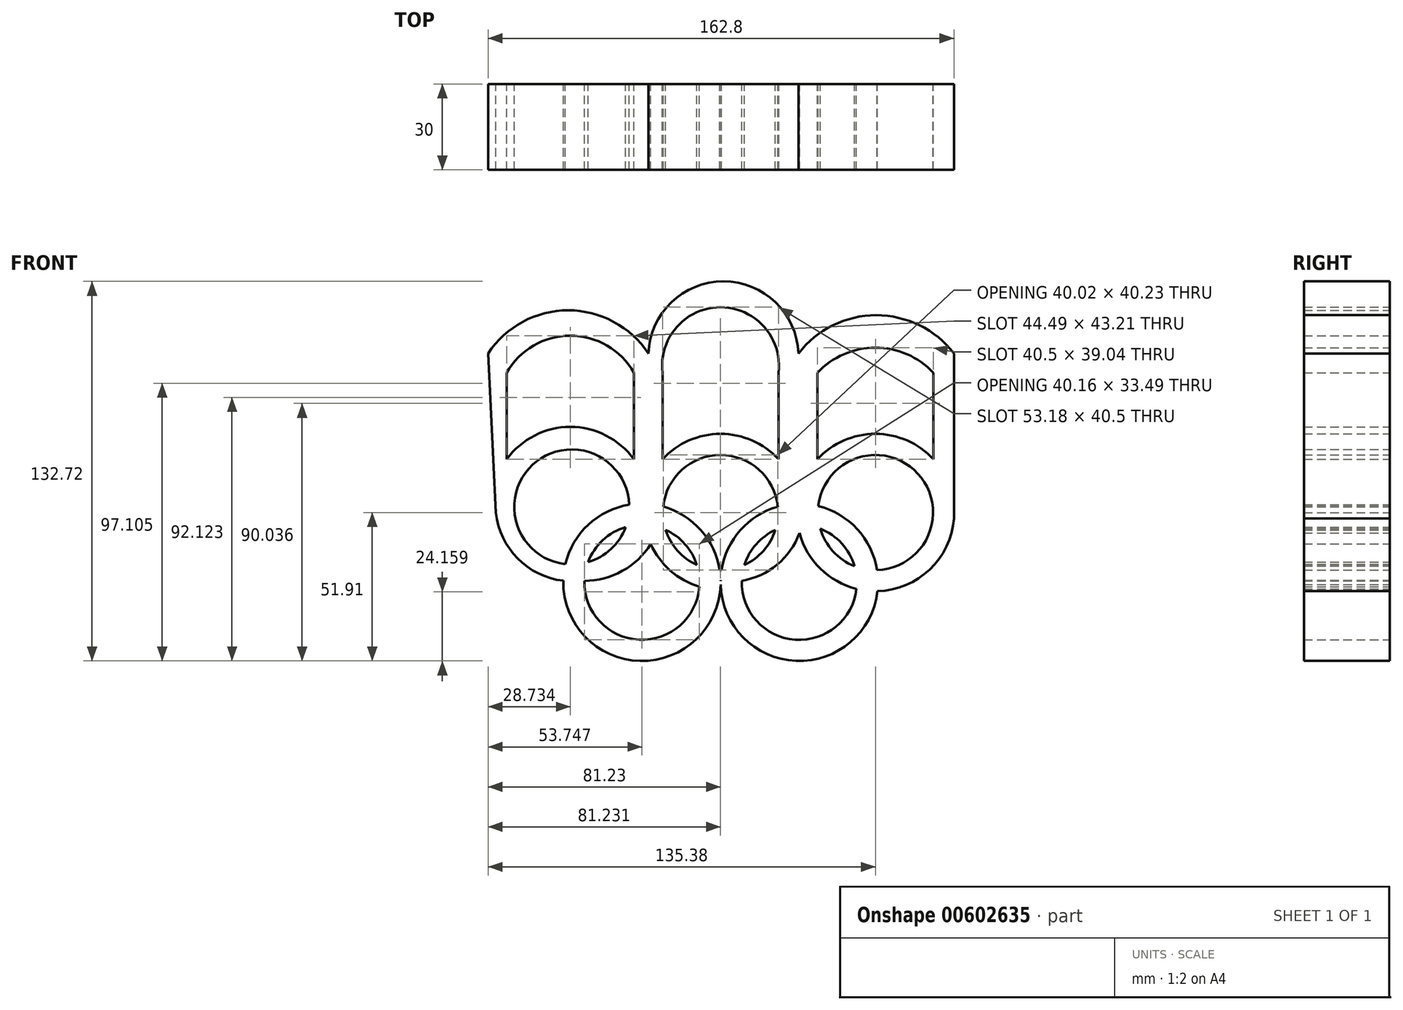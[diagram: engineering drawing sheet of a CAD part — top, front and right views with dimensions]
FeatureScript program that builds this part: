
annotation { "Feature Type Name" : "Feature", "Feature Type Description" : "" }
export const myFeature = defineFeature(function(context is Context, id is Id, definition is map)
    precondition{}
    {
        {
            var Q0;
            Q0=qCreatedBy(makeId("Front.planeOp"),FACE);
            var sketch = newSketch(context, id + "F0", { "sketchPlane" : qUnion([Q0])});
            skArc(sketch, "E0", {"start": v(-19.17, -6.08) * mm, "mid": v(-15.03, -13.36) * mm, "end": v(-8.28, -18.33) * mm});
            skArc(sketch, "E1", {"start": v(27.6, -7.19) * mm, "mid": v(34.9, -19.64) * mm, "end": v(47.5, -26.69) * mm});
            skArc(sketch, "E2", {"start": v(34.85, -5.68) * mm, "mid": v(39.32, -13.6) * mm, "end": v(46.82, -18.73) * mm});
            skArc(sketch, "E3", {"start": v(-31.88, 2.74) * mm, "mid": v(-65.68, 16.66) * mm, "end": v(-54.21, -18.05) * mm});
            skArc(sketch, "E4", {"start": v(-26.04, 3.06) * mm, "mid": v(-26.68, 3.08) * mm, "end": v(-27.33, 3.1) * mm});
            skArc(sketch, "E5", {"start": v(-26.39, -4.32) * mm, "mid": v(-26.47, -4.32) * mm, "end": v(-26.55, -4.31) * mm});
            skArc(sketch, "E6", {"start": v(0.03, -23.66) * mm, "mid": v(25.6, -51.84) * mm, "end": v(54.85, -27.5) * mm});
            skArc(sketch, "E7", {"start": v(7.42, -23.85) * mm, "mid": v(26.1, -44.47) * mm, "end": v(47.5, -26.69) * mm});
            skArc(sketch, "E8.trimOffspring", {"start": v(-31.88, 2.74) * mm, "mid": v(-46.2, -4.28) * mm, "end": v(-54.21, -18.05) * mm});
            skArc(sketch, "E9.trimOffspring", {"start": v(-33.14, -5.11) * mm, "mid": v(-41.16, -9.68) * mm, "end": v(-46.3, -17.36) * mm});
            skArc(sketch, "E10.trimOffspring", {"start": v(-47.56, -23.87) * mm, "mid": v(-28.48, -44.5) * mm, "end": v(-7.4, -25.92) * mm});
            skArc(sketch, "E11.trimOffspring", {"start": v(-46.3, -17.36) * mm, "mid": v(-38.27, -12.79) * mm, "end": v(-33.14, -5.11) * mm});
            skArc(sketch, "E12.trimOffspring", {"start": v(-54.95, -23.85) * mm, "mid": v(-27.36, -51.9) * mm, "end": v(0.03, -23.66) * mm});
            skArc(sketch, "E13.trimOffspring", {"start": v(-47.56, -23.87) * mm, "mid": v(-34.32, -20.42) * mm, "end": v(-24.38, -11) * mm});
            skArc(sketch, "E14.trimOffspring", {"start": v(-8.28, -18.33) * mm, "mid": v(-12.42, -11.04) * mm, "end": v(-19.17, -6.08) * mm});
            skArc(sketch, "E15.trimOffspring", {"start": v(-0.3, -20.11) * mm, "mid": v(0.03, -20.11) * mm, "end": v(0.36, -20.11) * mm});
            skArc(sketch, "E16.trimOffspring", {"start": v(0.03, -23.88) * mm, "mid": v(0.03, -23.88) * mm, "end": v(0.04, -23.88) * mm});
            skArc(sketch, "E17.trimOffspring", {"start": v(-0.3, -20.11) * mm, "mid": v(-6.9, -6.14) * mm, "end": v(-20, 2.07) * mm});
            skArc(sketch, "E18.trimOffspring", {"start": v(8.36, -18.3) * mm, "mid": v(15.05, -13.35) * mm, "end": v(19.16, -6.11) * mm});
            skArc(sketch, "E19.trimOffspring", {"start": v(19.16, -6.11) * mm, "mid": v(12.47, -11.06) * mm, "end": v(8.36, -18.3) * mm});
            skArc(sketch, "E20.trimOffspring", {"start": v(20, 2.05) * mm, "mid": v(0, 20.11) * mm, "end": v(-20, 2.07) * mm});
            skArc(sketch, "E21.trimOffspring", {"start": v(20, 2.05) * mm, "mid": v(6.95, -6.16) * mm, "end": v(0.36, -20.11) * mm});
            skArc(sketch, "E22.trimOffspring", {"start": v(20.25, 18.6) * mm, "mid": v(0, 27.5) * mm, "end": v(-20.25, 18.6) * mm});
            skArc(sketch, "E23.trimOffspring", {"start": v(27.33, 3.1) * mm, "mid": v(27.07, 3.1) * mm, "end": v(26.82, 3.08) * mm});
            skArc(sketch, "E24.trimOffspring", {"start": v(28.48, -4.31) * mm, "mid": v(27.73, -4.3) * mm, "end": v(26.99, -4.3) * mm});
            skArc(sketch, "E25.trimOffspring", {"start": v(46.82, -18.73) * mm, "mid": v(42.35, -10.82) * mm, "end": v(34.85, -5.68) * mm});
            skArc(sketch, "E26.trimOffspring", {"start": v(54.68, -20.1) * mm, "mid": v(68.98, 13.6) * mm, "end": v(34.17, 2.28) * mm});
            skArc(sketch, "E27.trimOffspring", {"start": v(54.85, -27.5) * mm, "mid": v(73.11, -19.92) * mm, "end": v(81.57, -2.05) * mm});
            skLineSegment(sketch, "E28", {"start": v(-78.48, 0) * mm, "end": v(-81.23, 55.6) * mm});
            skLineSegment(sketch, "E29", {"start": v(81.57, 2.05) * mm, "end": v(81.57, 55.6) * mm});
            skArc(sketch, "E30.trimOffspring", {"start": v(54.68, -20.1) * mm, "mid": v(47.8, -5.82) * mm, "end": v(34.17, 2.28) * mm});
            skPoint(sketch, "E31.orphan", {"position": v(-82, 71.15) * mm});
            skLineSegment(sketch, "E32", {"start": v(-74.74, 18.6) * mm, "end": v(-74.74, 48.91) * mm});
            skLineSegment(sketch, "E33", {"start": v(-30.25, 18.6) * mm, "end": v(-30.25, 48.91) * mm});
            skArc(sketch, "E34", {"start": v(-30.25, 48.91) * mm, "mid": v(-52.5, 61.82) * mm, "end": v(-74.74, 48.91) * mm});
            skArc(sketch, "E35.trimOffspring", {"start": v(-78.48, 0) * mm, "mid": v(-70.91, -16.07) * mm, "end": v(-54.95, -23.85) * mm});
            skArc(sketch, "E36.trimOffspring", {"start": v(-30.25, 18.6) * mm, "mid": v(-52.5, 29.94) * mm, "end": v(-74.74, 18.6) * mm});
            skLineSegment(sketch, "E37", {"start": v(-20.25, 18.6) * mm, "end": v(-20.25, 48.91) * mm});
            skLineSegment(sketch, "E38", {"start": v(20.25, 18.6) * mm, "end": v(20.25, 48.91) * mm});
            skPoint(sketch, "E39.start.orphan", {"position": v(-30.29, 55.6) * mm});
            skLineSegment(sketch, "E40", {"start": v(33.9, 18.6) * mm, "end": v(33.9, 48.91) * mm});
            skLineSegment(sketch, "E41", {"start": v(74.4, 18.6) * mm, "end": v(74.4, 48.91) * mm});
            skArc(sketch, "E42", {"start": v(74.4, 48.91) * mm, "mid": v(54.15, 57.65) * mm, "end": v(33.9, 48.91) * mm});
            skPoint(sketch, "E43.orphan", {"position": v(81.57, 67.5) * mm});
            skArc(sketch, "E44.trimOffspring", {"start": v(74.4, 18.6) * mm, "mid": v(54.15, 27.5) * mm, "end": v(33.9, 18.6) * mm});
            skArc(sketch, "E45", {"start": v(-25.23, 55.6) * mm, "mid": v(-53.23, 70.7) * mm, "end": v(-81.23, 55.6) * mm});
            skArc(sketch, "E46", {"start": v(27.27, 55.6) * mm, "mid": v(1.02, 80.8) * mm, "end": v(-25.23, 55.6) * mm});
            skArc(sketch, "E47", {"start": v(20.25, 48.91) * mm, "mid": v(0, 71.78) * mm, "end": v(-20.25, 48.91) * mm});
            skPoint(sketch, "E48.end.orphan", {"position": v(32.59, 55.6) * mm});
            skArc(sketch, "E49", {"start": v(81.57, 55.6) * mm, "mid": v(54.42, 69) * mm, "end": v(27.27, 55.6) * mm});
            skArc(sketch, "E50", {"start": v(-24.38, -11) * mm, "mid": v(-17.52, -20.32) * mm, "end": v(-7.4, -25.92) * mm});
            skArc(sketch, "E51", {"start": v(7.42, -23.85) * mm, "mid": v(19.77, -18.25) * mm, "end": v(27.6, -7.19) * mm});
            skLineSegment(sketch, "E52", {"start": v(81.57, 2.05) * mm, "end": v(81.57, -2.05) * mm});
            skSolve(sketch);
        }
        {
            var Q0;
            Q0 = qSketchRegion(id + "F0", true);
            extrude(context, id + "F1", {"entities" : qUnion([Q0]), "depth" : 30 * mm, "offsetDistance" : 25 * mm});
        }
    });
